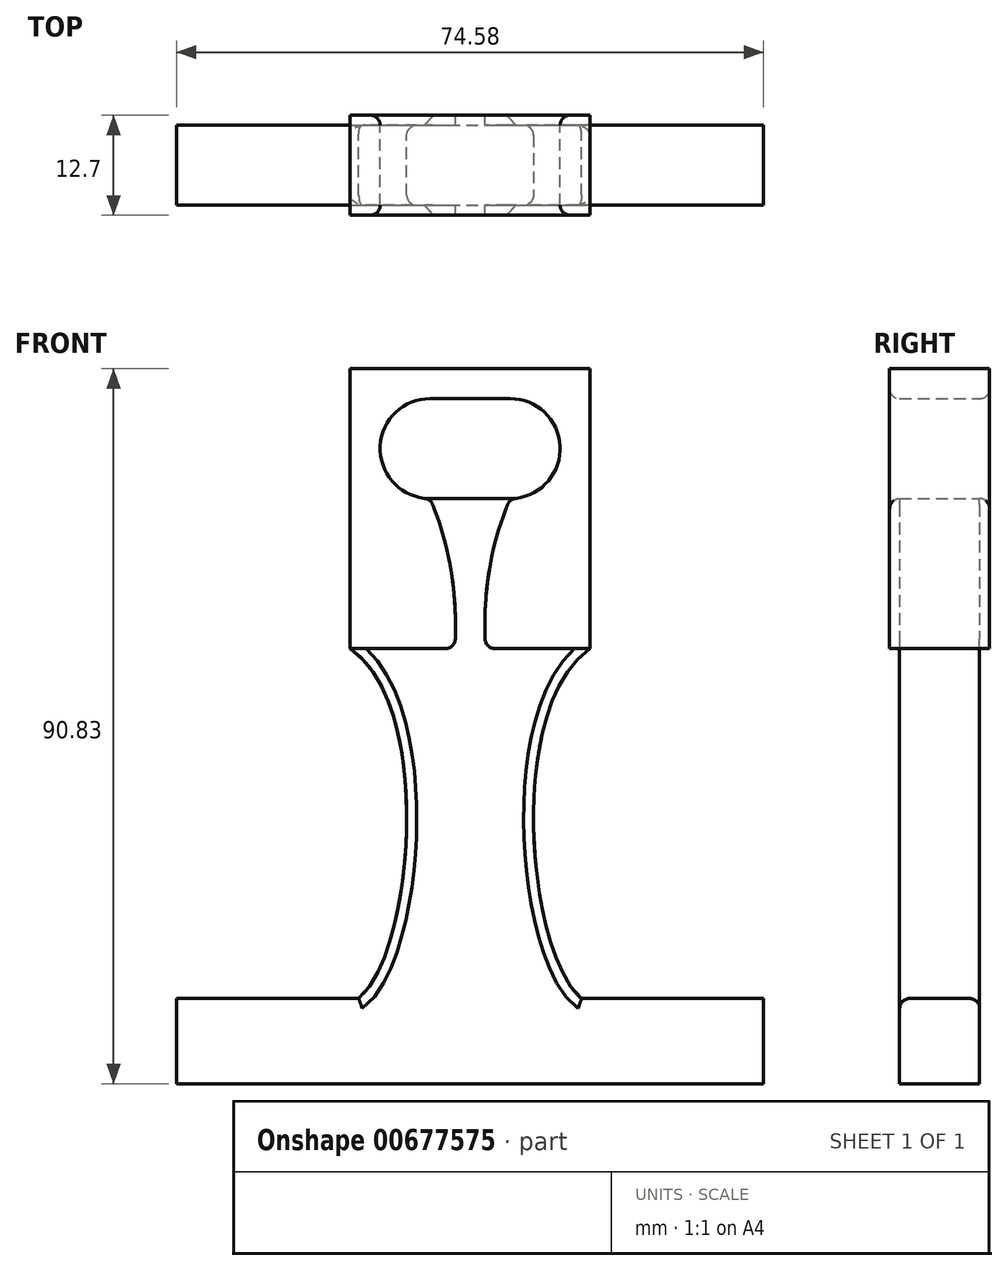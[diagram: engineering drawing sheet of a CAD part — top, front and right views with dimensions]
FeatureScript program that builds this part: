
annotation { "Feature Type Name" : "Feature", "Feature Type Description" : "" }
export const myFeature = defineFeature(function(context is Context, id is Id, definition is map)
    precondition{}
    {
        {
            var Q0;
            Q0=qCreatedBy(makeId("Front.planeOp"),FACE);
            var sketch = newSketch(context, id + "F0", { "sketchPlane" : qUnion([Q0])});
            skLineSegment(sketch, "E0", {"start": v(0, 10.16) * mm, "end": v(15.24, 10.16) * mm});
            skLineSegment(sketch, "E1", {"start": v(15.24, 10.16) * mm, "end": v(15.24, -25.4) * mm});
            skLineSegment(sketch, "E2", {"start": v(37.3, -69.85) * mm, "end": v(37.3, -80.67) * mm});
            skLineSegment(sketch, "E3", {"start": v(37.3, -80.67) * mm, "end": v(0, -80.67) * mm});
            skLineSegment(sketch, "E4.MirrorCS", {"start": v(-15.24, 10.16) * mm, "end": v(-15.24, -25.4) * mm});
            skLineSegment(sketch, "E5.MirrorCS", {"start": v(-37.3, -69.85) * mm, "end": v(-37.3, -80.67) * mm});
            skLineSegment(sketch, "E6.MirrorCS", {"start": v(0, 10.16) * mm, "end": v(-15.24, 10.16) * mm});
            skLineSegment(sketch, "E7.MirrorCS", {"start": v(-37.3, -80.67) * mm, "end": v(0, -80.67) * mm});
            skLineSegment(sketch, "E8", {"start": v(-37.3, -69.85) * mm, "end": v(-14.15, -69.85) * mm});
            skLineSegment(sketch, "E9.MirrorCS", {"start": v(37.3, -69.85) * mm, "end": v(14.15, -69.85) * mm});
            skCircle(sketch, "E10", {"center": v(5.08, 0) * mm, "radius": 6.35 * mm});
            skCircle(sketch, "E11.MirrorC", {"center": v(-5.08, 0) * mm, "radius": 6.35 * mm});
            skLineSegment(sketch, "E12", {"start": v(5.08, 6.35) * mm, "end": v(-5.08, 6.35) * mm});
            skLineSegment(sketch, "E13", {"start": v(-5.08, -6.35) * mm, "end": v(5.08, -6.35) * mm});
            skPoint(sketch, "E14", {"position": v(1.9, -25.4) * mm});
            skPoint(sketch, "E15.MirrorP", {"position": v(-1.9, -25.4) * mm});
            skLineSegment(sketch, "E16", {"start": v(-15.24, -25.4) * mm, "end": v(-1.9, -25.4) * mm});
            skLineSegment(sketch, "E17", {"start": v(1.9, -25.4) * mm, "end": v(15.24, -25.4) * mm});
            skFitSpline(sketch, "E18", {"points": [v(5.08, -6.35) * mm, v(1.9, -25.4) * mm], "startDerivative": vector(-11.33, -26.35) * mm, "endDerivative": vector(0.05, -7.83) * mm});
            skFitSpline(sketch, "E19.MirrorCS", {"points": [v(-5.08, -6.35) * mm, v(-1.9, -25.4) * mm], "startDerivative": vector(11.33, -26.35) * mm, "endDerivative": vector(-0.05, -7.83) * mm});
            skFitSpline(sketch, "E20", {"points": [v(-15.24, -25.4) * mm, v(-14.15, -69.85) * mm], "startDerivative": vector(32.64, -22.6) * mm, "endDerivative": vector(-20.35, -16.3) * mm});
            skFitSpline(sketch, "E21.MirrorCS", {"points": [v(15.24, -25.4) * mm, v(14.15, -69.85) * mm], "startDerivative": vector(-32.64, -22.6) * mm, "endDerivative": vector(20.35, -16.3) * mm});
            skSolve(sketch);
        }
        {
            var Q0;
            Q0=makeQuery(id+"F0.imprint","IMPRINT",FACE,{"disambiguationData":[TD([[makeQuery(id+"F0.imprint","IMPRINT",EDGE,{"derivedFrom":sQuery(id+"F0.wireOp",EDGE,"E0")}),-1.0]])]});
            extrude(context, id + "F1", {"entities" : qUnion([Q0]), "endBound" : BoundingType.SYMMETRIC, "depth" : 12.7 * mm, "offsetDistance" : 25.4 * mm});
        }
        {
            var Q0;
            Q0=makeQuery(id+"F0.imprint","IMPRINT",FACE,{"disambiguationData":[TD([[makeQuery(id+"F0.imprint","IMPRINT",EDGE,{"derivedFrom":sQuery(id+"F0.wireOp",EDGE,"E2")}),-1.0]])]});
            extrude(context, id + "F2", {"entities" : qUnion([Q0]), "operationType" : NewBodyOperationType.ADD, "endBound" : BoundingType.SYMMETRIC, "depth" : 10.16 * mm, "offsetDistance" : 25.4 * mm});
        }
        {
            var Q0;
            Q0=makeQuery(id+"F1.opExtrude","CAP_EDGE",EDGE,{"disambiguationData":[OSD([sQuery(id+"F0.wireOp",EDGE,"E10")])],"isStart":false});
            var Q1;
            Q1=makeQuery(id+"F1.opExtrude","CAP_EDGE",EDGE,{"disambiguationData":[OSD([sQuery(id+"F0.wireOp",EDGE,"E12")])],"isStart":false});
            var Q2;
            Q2=makeQuery(id+"F1.opExtrude","CAP_EDGE",EDGE,{"disambiguationData":[OSD([sQuery(id+"F0.wireOp",EDGE,"E11.MirrorC")])],"isStart":false});
            var Q3;
            {var subQ0=sQuery(id+"F0.wireOp",EDGE,"E19.MirrorCS");var subQ1=sQuery(id+"F0.wireOp",EDGE,"E18");var subQ2=sQuery(id+"F0.wireOp",EDGE,"E17");var subQ3=sQuery(id+"F0.wireOp",EDGE,"E16");var subQ4=sQuery(id+"F0.wireOp",EDGE,"E13");var subQ5=sQuery(id+"F0.wireOp",EDGE,"E10");Q3=makeQuery(id+"F2.boolean.opBoolean","SPLIT",EDGE,{"disambiguationData":[TD([makeQuery(id+"F1.opExtrude","CAP_FACE",FACE,{"disambiguationData":[OSD([sQuery(id+"F0.wireOp",EDGE,"E0"),sQuery(id+"F0.wireOp",EDGE,"E1"),sQuery(id+"F0.wireOp",EDGE,"E4.MirrorCS"),sQuery(id+"F0.wireOp",EDGE,"E6.MirrorCS"),subQ5,sQuery(id+"F0.wireOp",EDGE,"E11.MirrorC"),sQuery(id+"F0.wireOp",EDGE,"E12"),subQ3,subQ2,subQ1,subQ0])],"isStart":false})])],"derivedFrom":makeQuery(id+"F1.opExtrude","SWEPT_EDGE",EDGE,{"disambiguationData":[OSD([subQ5,subQ4,subQ1])]})});}
            var Q4;
            {var subQ0=sQuery(id+"F0.wireOp",EDGE,"E19.MirrorCS");var subQ1=sQuery(id+"F0.wireOp",EDGE,"E18");var subQ2=sQuery(id+"F0.wireOp",EDGE,"E17");var subQ3=sQuery(id+"F0.wireOp",EDGE,"E16");var subQ4=sQuery(id+"F0.wireOp",EDGE,"E13");var subQ5=sQuery(id+"F0.wireOp",EDGE,"E11.MirrorC");Q4=makeQuery(id+"F2.boolean.opBoolean","SPLIT",EDGE,{"disambiguationData":[TD([makeQuery(id+"F1.opExtrude","CAP_FACE",FACE,{"disambiguationData":[OSD([sQuery(id+"F0.wireOp",EDGE,"E0"),sQuery(id+"F0.wireOp",EDGE,"E1"),sQuery(id+"F0.wireOp",EDGE,"E4.MirrorCS"),sQuery(id+"F0.wireOp",EDGE,"E6.MirrorCS"),sQuery(id+"F0.wireOp",EDGE,"E10"),subQ5,sQuery(id+"F0.wireOp",EDGE,"E12"),subQ3,subQ2,subQ1,subQ0])],"isStart":false})])],"derivedFrom":makeQuery(id+"F1.opExtrude","SWEPT_EDGE",EDGE,{"disambiguationData":[OSD([subQ5,subQ4,subQ0])]})});}
            var Q5;
            Q5=makeQuery(id+"F1.opExtrude","CAP_EDGE",EDGE,{"disambiguationData":[OSD([sQuery(id+"F0.wireOp",EDGE,"E12")])],"isStart":true});
            var Q6;
            Q6=makeQuery(id+"F1.opExtrude","CAP_EDGE",EDGE,{"disambiguationData":[OSD([sQuery(id+"F0.wireOp",EDGE,"E10")])],"isStart":true});
            var Q7;
            Q7=makeQuery(id+"F1.opExtrude","CAP_EDGE",EDGE,{"disambiguationData":[OSD([sQuery(id+"F0.wireOp",EDGE,"E11.MirrorC")])],"isStart":true});
            var Q8;
            {var subQ0=sQuery(id+"F0.wireOp",EDGE,"E19.MirrorCS");var subQ1=sQuery(id+"F0.wireOp",EDGE,"E18");var subQ2=sQuery(id+"F0.wireOp",EDGE,"E17");var subQ3=sQuery(id+"F0.wireOp",EDGE,"E16");var subQ4=sQuery(id+"F0.wireOp",EDGE,"E13");var subQ5=sQuery(id+"F0.wireOp",EDGE,"E10");Q8=makeQuery(id+"F2.boolean.opBoolean","SPLIT",EDGE,{"disambiguationData":[TD([makeQuery(id+"F1.opExtrude","CAP_FACE",FACE,{"disambiguationData":[OSD([sQuery(id+"F0.wireOp",EDGE,"E0"),sQuery(id+"F0.wireOp",EDGE,"E1"),sQuery(id+"F0.wireOp",EDGE,"E4.MirrorCS"),sQuery(id+"F0.wireOp",EDGE,"E6.MirrorCS"),subQ5,sQuery(id+"F0.wireOp",EDGE,"E11.MirrorC"),sQuery(id+"F0.wireOp",EDGE,"E12"),subQ3,subQ2,subQ1,subQ0])],"isStart":true})])],"derivedFrom":makeQuery(id+"F1.opExtrude","SWEPT_EDGE",EDGE,{"disambiguationData":[OSD([subQ5,subQ4,subQ1])]})});}
            var Q9;
            {var subQ0=sQuery(id+"F0.wireOp",EDGE,"E19.MirrorCS");var subQ1=sQuery(id+"F0.wireOp",EDGE,"E18");var subQ2=sQuery(id+"F0.wireOp",EDGE,"E17");var subQ3=sQuery(id+"F0.wireOp",EDGE,"E16");var subQ4=sQuery(id+"F0.wireOp",EDGE,"E13");var subQ5=sQuery(id+"F0.wireOp",EDGE,"E11.MirrorC");Q9=makeQuery(id+"F2.boolean.opBoolean","SPLIT",EDGE,{"disambiguationData":[TD([makeQuery(id+"F1.opExtrude","CAP_FACE",FACE,{"disambiguationData":[OSD([sQuery(id+"F0.wireOp",EDGE,"E0"),sQuery(id+"F0.wireOp",EDGE,"E1"),sQuery(id+"F0.wireOp",EDGE,"E4.MirrorCS"),sQuery(id+"F0.wireOp",EDGE,"E6.MirrorCS"),sQuery(id+"F0.wireOp",EDGE,"E10"),subQ5,sQuery(id+"F0.wireOp",EDGE,"E12"),subQ3,subQ2,subQ1,subQ0])],"isStart":true})])],"derivedFrom":makeQuery(id+"F1.opExtrude","SWEPT_EDGE",EDGE,{"disambiguationData":[OSD([subQ5,subQ4,subQ0])]})});}
            var Q10;
            {var subQ0=sQuery(id+"F0.wireOp",EDGE,"E19.MirrorCS");var subQ1=sQuery(id+"F0.wireOp",EDGE,"E18");var subQ2=sQuery(id+"F0.wireOp",EDGE,"E17");var subQ3=sQuery(id+"F0.wireOp",EDGE,"E16");Q10=makeQuery(id+"F2.boolean.opBoolean","SPLIT",EDGE,{"disambiguationData":[TD([makeQuery(id+"F1.opExtrude","CAP_FACE",FACE,{"disambiguationData":[OSD([sQuery(id+"F0.wireOp",EDGE,"E0"),sQuery(id+"F0.wireOp",EDGE,"E1"),sQuery(id+"F0.wireOp",EDGE,"E4.MirrorCS"),sQuery(id+"F0.wireOp",EDGE,"E6.MirrorCS"),sQuery(id+"F0.wireOp",EDGE,"E10"),sQuery(id+"F0.wireOp",EDGE,"E11.MirrorC"),sQuery(id+"F0.wireOp",EDGE,"E12"),subQ3,subQ2,subQ1,subQ0])],"isStart":true})])],"derivedFrom":makeQuery(id+"F1.opExtrude","SWEPT_EDGE",EDGE,{"disambiguationData":[OSD([subQ3,subQ0])]})});}
            var Q11;
            {var subQ0=sQuery(id+"F0.wireOp",EDGE,"E19.MirrorCS");var subQ1=sQuery(id+"F0.wireOp",EDGE,"E18");var subQ2=sQuery(id+"F0.wireOp",EDGE,"E17");var subQ3=sQuery(id+"F0.wireOp",EDGE,"E16");Q11=makeQuery(id+"F2.boolean.opBoolean","SPLIT",EDGE,{"disambiguationData":[TD([makeQuery(id+"F1.opExtrude","CAP_FACE",FACE,{"disambiguationData":[OSD([sQuery(id+"F0.wireOp",EDGE,"E0"),sQuery(id+"F0.wireOp",EDGE,"E1"),sQuery(id+"F0.wireOp",EDGE,"E4.MirrorCS"),sQuery(id+"F0.wireOp",EDGE,"E6.MirrorCS"),sQuery(id+"F0.wireOp",EDGE,"E10"),sQuery(id+"F0.wireOp",EDGE,"E11.MirrorC"),sQuery(id+"F0.wireOp",EDGE,"E12"),subQ3,subQ2,subQ1,subQ0])],"isStart":true})])],"derivedFrom":makeQuery(id+"F1.opExtrude","SWEPT_EDGE",EDGE,{"disambiguationData":[OSD([subQ2,subQ1])]})});}
            var Q12;
            {var subQ0=sQuery(id+"F0.wireOp",EDGE,"E19.MirrorCS");var subQ1=sQuery(id+"F0.wireOp",EDGE,"E18");var subQ2=sQuery(id+"F0.wireOp",EDGE,"E17");var subQ3=sQuery(id+"F0.wireOp",EDGE,"E16");Q12=makeQuery(id+"F2.boolean.opBoolean","SPLIT",EDGE,{"disambiguationData":[TD([makeQuery(id+"F1.opExtrude","CAP_FACE",FACE,{"disambiguationData":[OSD([sQuery(id+"F0.wireOp",EDGE,"E0"),sQuery(id+"F0.wireOp",EDGE,"E1"),sQuery(id+"F0.wireOp",EDGE,"E4.MirrorCS"),sQuery(id+"F0.wireOp",EDGE,"E6.MirrorCS"),sQuery(id+"F0.wireOp",EDGE,"E10"),sQuery(id+"F0.wireOp",EDGE,"E11.MirrorC"),sQuery(id+"F0.wireOp",EDGE,"E12"),subQ3,subQ2,subQ1,subQ0])],"isStart":false})])],"derivedFrom":makeQuery(id+"F1.opExtrude","SWEPT_EDGE",EDGE,{"disambiguationData":[OSD([subQ3,subQ0])]})});}
            var Q13;
            {var subQ0=sQuery(id+"F0.wireOp",EDGE,"E19.MirrorCS");var subQ1=sQuery(id+"F0.wireOp",EDGE,"E18");var subQ2=sQuery(id+"F0.wireOp",EDGE,"E17");var subQ3=sQuery(id+"F0.wireOp",EDGE,"E16");Q13=makeQuery(id+"F2.boolean.opBoolean","SPLIT",EDGE,{"disambiguationData":[TD([makeQuery(id+"F1.opExtrude","CAP_FACE",FACE,{"disambiguationData":[OSD([sQuery(id+"F0.wireOp",EDGE,"E0"),sQuery(id+"F0.wireOp",EDGE,"E1"),sQuery(id+"F0.wireOp",EDGE,"E4.MirrorCS"),sQuery(id+"F0.wireOp",EDGE,"E6.MirrorCS"),sQuery(id+"F0.wireOp",EDGE,"E10"),sQuery(id+"F0.wireOp",EDGE,"E11.MirrorC"),sQuery(id+"F0.wireOp",EDGE,"E12"),subQ3,subQ2,subQ1,subQ0])],"isStart":false})])],"derivedFrom":makeQuery(id+"F1.opExtrude","SWEPT_EDGE",EDGE,{"disambiguationData":[OSD([subQ2,subQ1])]})});}
            var Q14;
            Q14=makeQuery(id+"F2.opExtrude","CAP_EDGE",EDGE,{"disambiguationData":[OSD([sQuery(id+"F0.wireOp",EDGE,"E21.MirrorCS")])],"isStart":false});
            var Q15;
            Q15=makeQuery(id+"F2.opExtrude","CAP_EDGE",EDGE,{"disambiguationData":[OSD([sQuery(id+"F0.wireOp",EDGE,"E20")])],"isStart":false});
            var Q16;
            Q16=makeQuery(id+"F2.opExtrude","CAP_EDGE",EDGE,{"disambiguationData":[OSD([sQuery(id+"F0.wireOp",EDGE,"E21.MirrorCS")])],"isStart":true});
            var Q17;
            Q17=makeQuery(id+"F2.opExtrude","CAP_EDGE",EDGE,{"disambiguationData":[OSD([sQuery(id+"F0.wireOp",EDGE,"E20")])],"isStart":true});
            var Q18;
            Q18=makeQuery(id+"F2.opExtrude","CAP_EDGE",EDGE,{"disambiguationData":[OSD([sQuery(id+"F0.wireOp",EDGE,"E9.MirrorCS")])],"isStart":true});
            var Q19;
            Q19=makeQuery(id+"F2.opExtrude","CAP_EDGE",EDGE,{"disambiguationData":[OSD([sQuery(id+"F0.wireOp",EDGE,"E9.MirrorCS")])],"isStart":false});
            var Q20;
            Q20=makeQuery(id+"F2.opExtrude","CAP_EDGE",EDGE,{"disambiguationData":[OSD([sQuery(id+"F0.wireOp",EDGE,"E8")])],"isStart":false});
            var Q21;
            Q21=makeQuery(id+"F2.opExtrude","CAP_EDGE",EDGE,{"disambiguationData":[OSD([sQuery(id+"F0.wireOp",EDGE,"E8")])],"isStart":true});
            fillet(context, id + "F3", {"entities" : qUnion([Q0, Q1, Q2, Q3, Q4, Q5, Q6, Q7, Q8, Q9, Q10, Q11, Q12, Q13, Q14, Q15, Q16, Q17, Q18, Q19, Q20, Q21]), "radius" : 1.27 * mm, "tangentPropagation" : true, "allowEdgeOverflow" : false});
        }
    });
